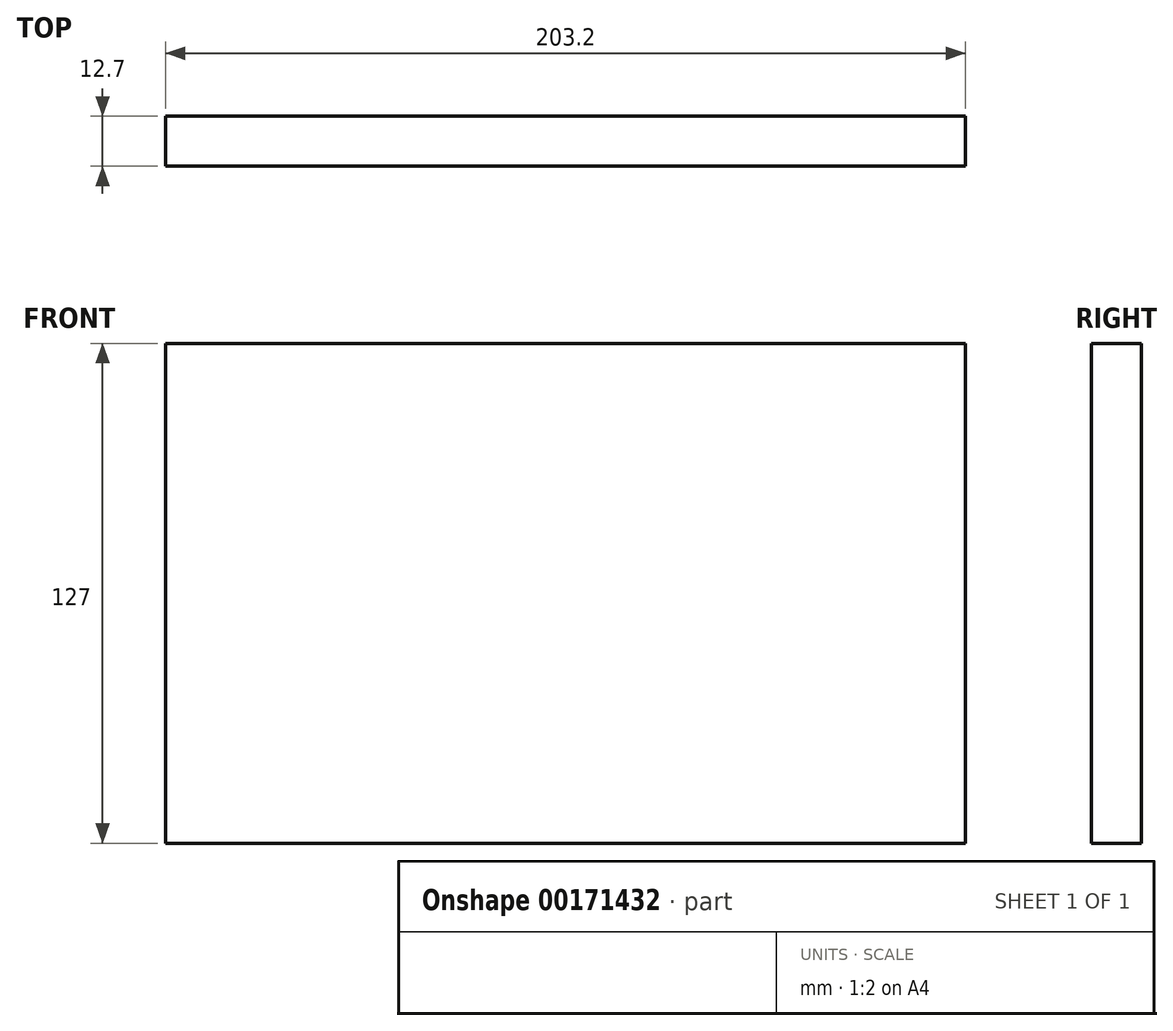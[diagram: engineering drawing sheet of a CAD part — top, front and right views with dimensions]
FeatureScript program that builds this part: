
annotation { "Feature Type Name" : "Feature", "Feature Type Description" : "" }
export const myFeature = defineFeature(function(context is Context, id is Id, definition is map)
    precondition{}
    {
        {
            var Q0;
            Q0=qCreatedBy(makeId("Front.planeOp"),FACE);
            var sketch = newSketch(context, id + "F0", { "sketchPlane" : qUnion([Q0])});
            skLineSegment(sketch, "E0.bottom", {"start": v(101.6, 63.5) * mm, "end": v(-101.6, 63.5) * mm});
            skLineSegment(sketch, "E0.top", {"start": v(101.6, -63.5) * mm, "end": v(-101.6, -63.5) * mm});
            skLineSegment(sketch, "E0.left", {"start": v(101.6, 63.5) * mm, "end": v(101.6, -63.5) * mm});
            skLineSegment(sketch, "E0.right", {"start": v(-101.6, 63.5) * mm, "end": v(-101.6, -63.5) * mm});
            skPoint(sketch, "E0.middle", {"position": v(0, 0) * mm});
            skSolve(sketch);
        }
        {
            var Q0;
            Q0 = qSketchRegion(id + "F0", true);
            extrude(context, id + "F1", {"entities" : qUnion([Q0]), "oppositeDirection" : true, "depth" : 127 * mm});
        }
        {
            var Q0;
            Q0=makeQuery(id+"F1.opExtrude","SWEPT_FACE",FACE,{"disambiguationData":[OSD([sQuery(id+"F0.wireOp",EDGE,"E0.bottom")])]});
            var Q1;
            Q1=makeQuery(id+"F1.opExtrude","CAP_FACE",FACE,{"disambiguationData":[OSD([sQuery(id+"F0.wireOp",EDGE,"E0.bottom"),sQuery(id+"F0.wireOp",EDGE,"E0.top"),sQuery(id+"F0.wireOp",EDGE,"E0.left"),sQuery(id+"F0.wireOp",EDGE,"E0.right")])],"isStart":true});
            var Q2;
            Q2=makeQuery(id+"F1.opExtrude","SWEPT_FACE",FACE,{"disambiguationData":[OSD([sQuery(id+"F0.wireOp",EDGE,"E0.left")])]});
            var Q3;
            Q3=makeQuery(id+"F1.opExtrude","SWEPT_FACE",FACE,{"disambiguationData":[OSD([sQuery(id+"F0.wireOp",EDGE,"E0.right")])]});
            var Q4;
            Q4=makeQuery(id+"F1.opExtrude","SWEPT_FACE",FACE,{"disambiguationData":[OSD([sQuery(id+"F0.wireOp",EDGE,"E0.top")])]});
            shell(context, id + "F2", {"entities" : qUnion([Q0, Q1, Q2, Q3, Q4]), "thickness" : 12.7 * mm});
        }
    });
